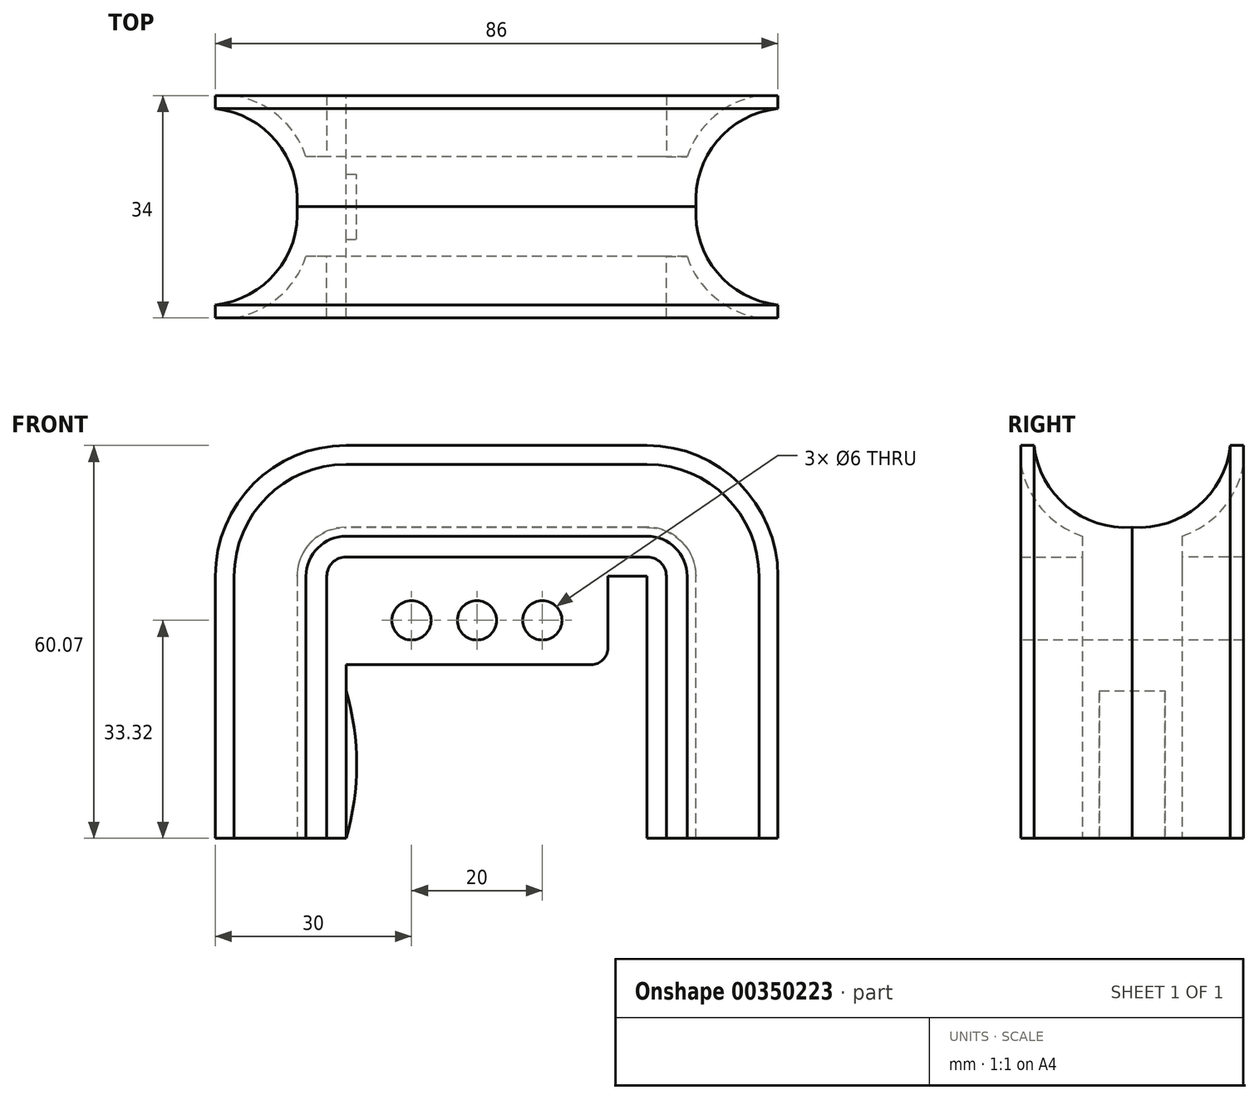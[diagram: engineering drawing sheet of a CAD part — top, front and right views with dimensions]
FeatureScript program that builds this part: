
annotation { "Feature Type Name" : "Feature", "Feature Type Description" : "" }
export const myFeature = defineFeature(function(context is Context, id is Id, definition is map)
    precondition{}
    {
        {
            var Q0;
            Q0=qCreatedBy(makeId("Front.planeOp"),FACE);
            var sketch = newSketch(context, id + "F0", { "sketchPlane" : qUnion([Q0])});
            skLineSegment(sketch, "E0.bottom", {"start": v(0, 0) * mm, "end": v(-40, 0) * mm});
            skLineSegment(sketch, "E0.top", {"start": v(0, 4) * mm, "end": v(-40, 4) * mm});
            skLineSegment(sketch, "E0.right", {"start": v(-40, 0) * mm, "end": v(-40, 4) * mm});
            skLineSegment(sketch, "E1.bottom", {"start": v(0, 17.5) * mm, "end": v(6, 17.5) * mm});
            skLineSegment(sketch, "E1.top", {"start": v(0, -83.02) * mm, "end": v(6, -83.02) * mm});
            skLineSegment(sketch, "E1.left", {"start": v(0, 17.5) * mm, "end": v(0, 4) * mm});
            skLineSegment(sketch, "E1.right", {"start": v(6, 17.5) * mm, "end": v(6, -83.02) * mm});
            skLineSegment(sketch, "E2.trimOffspring", {"start": v(0, 0) * mm, "end": v(0, -83.02) * mm});
            skLineSegment(sketch, "E3", {"start": v(-40, 0) * mm, "end": v(-40, -22.57) * mm});
            skArc(sketch, "E4", {"start": v(-40, -22.57) * mm, "mid": v(-38.4, -11.29) * mm, "end": v(-40, 0) * mm});
            skLineSegment(sketch, "E5", {"start": v(-40, -22.57) * mm, "end": v(-60, -22.57) * mm});
            skLineSegment(sketch, "E6", {"start": v(6, -22.57) * mm, "end": v(26, -22.57) * mm});
            skArc(sketch, "E7", {"start": v(26, 17.5) * mm, "mid": v(20.14, 31.64) * mm, "end": v(6, 37.5) * mm});
            skArc(sketch, "E8", {"start": v(-60, 17.5) * mm, "mid": v(-54.14, 31.64) * mm, "end": v(-40, 37.5) * mm});
            skLineSegment(sketch, "E9", {"start": v(-60, -22.57) * mm, "end": v(-60, 17.5) * mm});
            skLineSegment(sketch, "E10", {"start": v(-40, 37.5) * mm, "end": v(6, 37.5) * mm});
            skLineSegment(sketch, "E11", {"start": v(26, 17.5) * mm, "end": v(26, -22.57) * mm});
            skLineSegment(sketch, "E12", {"start": v(-40, 17.5) * mm, "end": v(-40, 4) * mm, "construction": true});
            skLineSegment(sketch, "E13", {"start": v(-40, 10.75) * mm, "end": v(0, 10.75) * mm, "construction": true});
            skPoint(sketch, "E14", {"position": v(-20, 10.75) * mm});
            skPoint(sketch, "E15", {"position": v(-30, 10.75) * mm});
            skPoint(sketch, "E16", {"position": v(-10, 10.75) * mm});
            skSolve(sketch);
        }
        {
            var Q0;
            Q0=makeQuery(id+"F0.imprint","IMPRINT",FACE,{"disambiguationData":[TD([[makeQuery(id+"F0.imprint","IMPRINT",EDGE,{"derivedFrom":sQuery(id+"F0.wireOp",EDGE,"E0.top")}),-1.0]])]});
            extrude(context, id + "F1", {"entities" : qUnion([Q0]), "endBound" : BoundingType.SYMMETRIC, "depth" : 34 * mm});
        }
        {
            var Q0;
            Q0=makeQuery(id+"F0.imprint","IMPRINT",FACE,{"disambiguationData":[TD([[makeQuery(id+"F0.imprint","IMPRINT",EDGE,{"derivedFrom":sQuery(id+"F0.wireOp",EDGE,"E3")}),1.0]])]});
            extrude(context, id + "F2", {"entities" : qUnion([Q0]), "operationType" : NewBodyOperationType.ADD, "endBound" : BoundingType.SYMMETRIC, "depth" : 10 * mm});
        }
        {
            var Q0;
            Q0=makeQuery(id+"F1.opExtrude","SWEPT_FACE",FACE,{"disambiguationData":[OSD([sQuery(id+"F0.wireOp",EDGE,"E6")])]});
            var sketch = newSketch(context, id + "F3", { "sketchPlane" : qUnion([Q0])});
            skArc(sketch, "E17", {"start": v(26, 15) * mm, "mid": v(16.7, 10.04) * mm, "end": v(13.5, 0) * mm});
            skPoint(sketch, "E17.endSnap0", {"position": v(26, 0) * mm});
            skArc(sketch, "E18.MirrorCS", {"start": v(26, -15) * mm, "mid": v(16.7, -10.04) * mm, "end": v(13.5, 0) * mm});
            skLineSegment(sketch, "E19", {"start": v(8.95, 17) * mm, "end": v(8.95, 7.62) * mm});
            skLineSegment(sketch, "E20", {"start": v(8.95, 7.62) * mm, "end": v(12.12, 7.62) * mm});
            skArc(sketch, "E21", {"start": v(23.12, 17) * mm, "mid": v(16.32, 13.84) * mm, "end": v(12.12, 7.62) * mm});
            skLineSegment(sketch, "E22", {"start": v(8.95, 17) * mm, "end": v(23.12, 17) * mm});
            skLineSegment(sketch, "E23.MirrorCS", {"start": v(8.95, -17) * mm, "end": v(23.12, -17) * mm});
            skArc(sketch, "E24.MirrorCS", {"start": v(23.12, -17) * mm, "mid": v(16.32, -13.84) * mm, "end": v(12.12, -7.62) * mm});
            skLineSegment(sketch, "E25.MirrorCS", {"start": v(8.95, -17) * mm, "end": v(8.95, -7.62) * mm});
            skLineSegment(sketch, "E26.MirrorCS", {"start": v(8.95, -7.62) * mm, "end": v(12.12, -7.62) * mm});
            skSolve(sketch);
        }
        {
            var Q0;
            {var subQ0=sQuery(id+"F3.wireOp",EDGE,"E17");Q0=makeQuery(id+"F3.imprint","IMPRINT",FACE,{"disambiguationData":[TD([[makeQuery(id+"F3.imprint","IMPRINT",EDGE,{"derivedFrom":subQ0}),1.0]])]});}
            var Q1;
            Q1=makeQuery(id+"F3.imprint","IMPRINT",FACE,{"disambiguationData":[TD([[makeQuery(id+"F3.imprint","IMPRINT",EDGE,{"derivedFrom":sQuery(id+"F3.wireOp",EDGE,"E19")}),1.0]])]});
            var Q2;
            Q2=makeQuery(id+"F3.imprint","IMPRINT",FACE,{"disambiguationData":[TD([[makeQuery(id+"F3.imprint","IMPRINT",EDGE,{"derivedFrom":sQuery(id+"F3.wireOp",EDGE,"E23.MirrorCS")}),1.0]])]});
            var Q3;
            Q3=sQuery(id+"F0.wireOp",EDGE,"E11");
            var Q4;
            Q4=sQuery(id+"F0.wireOp",EDGE,"E7");
            var Q5;
            Q5=sQuery(id+"F0.wireOp",EDGE,"E10");
            var Q6;
            Q6=sQuery(id+"F0.wireOp",EDGE,"E8");
            var Q7;
            Q7=sQuery(id+"F0.wireOp",EDGE,"E9");
            sweep(context, id + "F4", {"operationType" : NewBodyOperationType.REMOVE, "profiles" : qUnion([Q0, Q1, Q2]), "path" : qUnion([Q3, Q4, Q5, Q6, Q7])});
        }
        {
            var Q0;
            Q0=sQuery(id+"F0.wireOp",VERTEX,"E15");
            var Q1;
            Q1=sQuery(id+"F0.wireOp",VERTEX,"E14");
            var Q2;
            Q2=sQuery(id+"F0.wireOp",VERTEX,"E16");
            var Q3;
            Q3=makeQuery(id+"F1.opExtrude","SWEPT_BODY",BODY,{"disambiguationData":[OSD([sQuery(id+"F0.wireOp",EDGE,"E0.top"),sQuery(id+"F0.wireOp",EDGE,"E0.right"),sQuery(id+"F0.wireOp",EDGE,"E1.bottom"),sQuery(id+"F0.wireOp",EDGE,"E1.left"),sQuery(id+"F0.wireOp",EDGE,"E1.right"),sQuery(id+"F0.wireOp",EDGE,"E3"),sQuery(id+"F0.wireOp",EDGE,"E5"),sQuery(id+"F0.wireOp",EDGE,"E6"),sQuery(id+"F0.wireOp",EDGE,"E7"),sQuery(id+"F0.wireOp",EDGE,"E8"),sQuery(id+"F0.wireOp",EDGE,"E9"),sQuery(id+"F0.wireOp",EDGE,"E10"),sQuery(id+"F0.wireOp",EDGE,"E11")])]});
            hole(context, id + "F5", {"style" : HoleStyle.SIMPLE, "endStyle" : HoleEndStyle.THROUGH, "holeDiameter" : 6 * mm, "isTappedThrough" : true, "tappedDepth" : 12 * mm, "tapClearance" : 3, "startFromSketch" : true, "locations" : qUnion([Q0, Q1, Q2]), "scope" : qUnion([Q3])});
        }
        {
            var Q0;
            Q0=sQuery(id+"F0.wireOp",VERTEX,"E16");
            var Q1;
            Q1=sQuery(id+"F0.wireOp",VERTEX,"E14");
            var Q2;
            Q2=sQuery(id+"F0.wireOp",VERTEX,"E15");
            var Q3;
            Q3=makeQuery(id+"F1.opExtrude","SWEPT_BODY",BODY,{"disambiguationData":[OSD([sQuery(id+"F0.wireOp",EDGE,"E0.top"),sQuery(id+"F0.wireOp",EDGE,"E0.right"),sQuery(id+"F0.wireOp",EDGE,"E1.bottom"),sQuery(id+"F0.wireOp",EDGE,"E1.left"),sQuery(id+"F0.wireOp",EDGE,"E1.right"),sQuery(id+"F0.wireOp",EDGE,"E3"),sQuery(id+"F0.wireOp",EDGE,"E5"),sQuery(id+"F0.wireOp",EDGE,"E6"),sQuery(id+"F0.wireOp",EDGE,"E7"),sQuery(id+"F0.wireOp",EDGE,"E8"),sQuery(id+"F0.wireOp",EDGE,"E9"),sQuery(id+"F0.wireOp",EDGE,"E10"),sQuery(id+"F0.wireOp",EDGE,"E11")])]});
            hole(context, id + "F6", {"style" : HoleStyle.SIMPLE, "endStyle" : HoleEndStyle.THROUGH, "oppositeDirection" : true, "holeDiameter" : 6 * mm, "isTappedThrough" : true, "tappedDepth" : 12 * mm, "tapClearance" : 3, "startFromSketch" : true, "locations" : qUnion([Q0, Q1, Q2]), "scope" : qUnion([Q3])});
        }
        {
            var Q0;
            Q0=makeQuery(id+"F1.opExtrude","SWEPT_EDGE",EDGE,{"disambiguationData":[OSD([sQuery(id+"F0.wireOp",EDGE,"E0.top"),sQuery(id+"F0.wireOp",EDGE,"E1.left")])]});
            fillet(context, id + "F7", {"entities" : qUnion([Q0]), "radius" : 2.5 * mm, "tangentPropagation" : true, "allowEdgeOverflow" : false});
        }
    });
